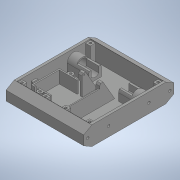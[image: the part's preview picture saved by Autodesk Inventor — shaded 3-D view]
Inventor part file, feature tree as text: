
AUTODESK INVENTOR PART (.ipt)
format: ipt  version: 2020 (Build 240168000, 168)  size: 623,104 bytes
history: native  units: in
note: dims shown in document units (in); Inventor stores cm internally (conversion verified against a paired STEP export)
features: extrude x18, sketch x18, projected_geometry x14, mirror x6, plane x1
ambient origin geometry x8: Origin, YZ Plane, XZ Plane, XY Plane, X Axis, Y Axis, Z Axis, Center Point
bodies: Solid1 (feature_tree)
feature tree (57):
  extrude  "Extrusion1"  Depth=5.6693in
  extrude  "Extrusion2"  TaperAngle=0.0deg  [1 undecoded]
  extrude  "Extrusion3"  Depth=1.063in
  extrude  "Extrusion4"  Depth=0.315in
  extrude  "Extrusion5"  TaperAngle=0.0deg  [1 undecoded]
  extrude  "Extrusion6"  Depth=0.5906in
  mirror  "Mirror1"
  extrude  "Extrusion7"  Depth=0.0787in
  mirror  "Mirror2"
  extrude  "Extrusion8"  Depth=0.6102in
  mirror  "Mirror3"
  plane  "Work Plane1"
  extrude  "Extrusion9"  Depth=0.7874in TaperAngle=0.0deg
  mirror  "Mirror4"
  extrude  "Extrusion10"  Depth=6.063in TaperAngle=0.0deg
  extrude  "Extrusion11"  Depth=0.1575in
  extrude  "Extrusion12"  TaperAngle=0.0deg  [1 undecoded]
  extrude  "Extrusion13"  Depth=0.2756in
  extrude  "Extrusion14"  Depth=0.4331in
  extrude  "Extrusion17"  Depth=2.7559in
  extrude  "Extrusion18"  Depth=0.0413in
  mirror  "Mirror6"
  extrude  "Extrusion19"  TaperAngle=0.0deg  [1 undecoded]
  mirror  "Mirror7"
  extrude  "Extrusion20"  Depth=0.0787in
  sketch  "Sketch1"  dims[d0=1.1811in d1=5.6693in]
  sketch  "Sketch2"  dims[d2=4.8819in d3=0.0in]
  projected_geometry  "Projected Loop1"
  sketch  "Sketch3"  dims[d4=0.1575in d5=1.063in]
  projected_geometry  "Projected Loop2"
  projected_geometry  "Projected Loop3"
  sketch  "Sketch4"  dims[d6=0.0in d8=0.315in]
  sketch  "Sketch5"  dims[d10=0.993in d11=0.0in]
  projected_geometry  "Projected Loop4"
  sketch  "Sketch6"  dims[d12=0.6496in d13=0.5906in]
  sketch  "Sketch7"  dims[d14=1.5748in d15=0.0787in]
  sketch  "Sketch9"  dims[d16=0.5512in d17=0.0in d18=0.6102in]
  sketch  "Sketch10"  dims[d19=0.4803in d20=0.7874in d21=0.0in]
  sketch  "Sketch12"  dims[d22=0.1654in d23=6.063in d24=0.0in]
  projected_geometry  "Projected Loop6"
  projected_geometry  "Projected Loop7"
  projected_geometry  "Projected Loop8"
  sketch  "Sketch13"  dims[d25=0.5114in d26=0.1575in]
  sketch  "Sketch14"  dims[d27=1.5748in d28=0.0in d29=0.0in]
  sketch  "Sketch15"  dims[d30=0.1575in d31=0.2756in]
  projected_geometry  "Projected Loop15"
  sketch  "Sketch16"  dims[d32=0.0in d33=0.4331in]
  projected_geometry  "Projected Loop19"
  projected_geometry  "Projected Loop20"
  projected_geometry  "Projected Loop21"
  projected_geometry  "Projected Loop22"
  projected_geometry  "Projected Loop23"
  projected_geometry  "Projected Loop24"
  sketch  "Sketch20"  dims[d34=0.0827in d38=2.7559in]
  sketch  "Sketch21"  dims[d40=0.0413in d41=0.0909in]
  sketch  "Sketch22"  dims[d42=0.2362in d43=0.0in]
  sketch  "Sketch23"  dims[d44=60.0deg d45=0.0787in d46=0.315in d48=0.993in d49=0.0in d53=0.2756in d54=0.0in d55=0.4724in d56=1.2008in d57=1.6142in d58=1.5945in d59=0.0787in d60=0.0787in d62=0.315in d63=0.7677in d64=0.0in d66=0.1476in d67=0.2756in d68=0.0in d69=0.7874in d70=0.2953in d71=0.1181in d72=0.0in d89=0.0157in d90=0.0157in d91=0.1476in d92=0.1476in d96=0.315in d97=0.1575in d98=0.1181in d99=0.0in d102=0.1772in d104=0.3346in d105=135.0deg d106=0.2362in d107=0.0in d108=0.0394in d109=0.0in d110=0.063in d111=0.0394in d112=0.0in]
note: 4 required parameter values undecoded (feature->parameter linkage not recoverable at this tier; creation-order binding heuristic only, values carry confidence <= 0.55)
